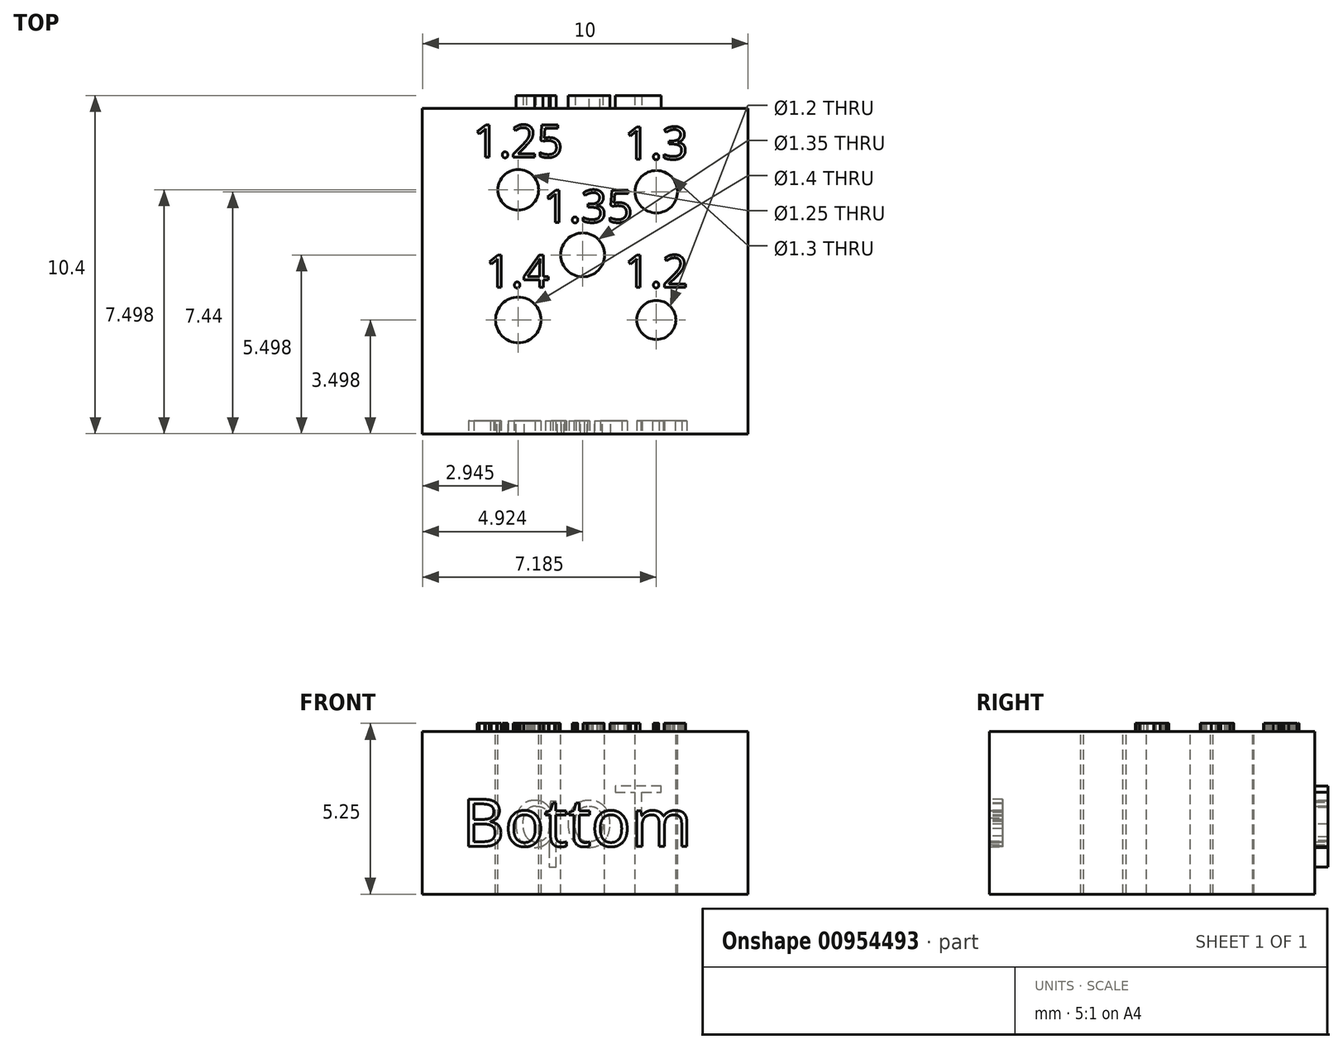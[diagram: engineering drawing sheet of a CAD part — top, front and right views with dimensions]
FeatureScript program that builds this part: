
annotation { "Feature Type Name" : "Feature", "Feature Type Description" : "" }
export const myFeature = defineFeature(function(context is Context, id is Id, definition is map)
    precondition{}
    {
        {
            var Q0;
            Q0=qCreatedBy(makeId("Top.planeOp"),FACE);
            var sketch = newSketch(context, id + "F0", { "sketchPlane" : qUnion([Q0])});
            skLineSegment(sketch, "E0.bottom", {"start": v(-5.65, 2.56) * mm, "end": v(4.35, 2.56) * mm});
            skLineSegment(sketch, "E0.top", {"start": v(-5.65, -7.44) * mm, "end": v(4.35, -7.44) * mm});
            skLineSegment(sketch, "E0.left", {"start": v(-5.65, 2.56) * mm, "end": v(-5.65, -7.44) * mm});
            skLineSegment(sketch, "E0.right", {"start": v(4.35, 2.56) * mm, "end": v(4.35, -7.44) * mm});
            skSolve(sketch);
        }
        {
            var Q0;
            Q0=makeQuery(id+"F0.imprint","IMPRINT",FACE,{"disambiguationData":[TD([[makeQuery(id+"F0.imprint","IMPRINT",EDGE,{"derivedFrom":sQuery(id+"F0.wireOp",EDGE,"E0.bottom")}),-1.0]])]});
            extrude(context, id + "F1", {"entities" : qUnion([Q0]), "depth" : 5 * mm, "offsetDistance" : 25 * mm});
        }
        {
            var Q0;
            Q0=makeQuery(id+"F1.opExtrude","CAP_FACE",FACE,{"disambiguationData":[OSD([sQuery(id+"F0.wireOp",EDGE,"E0.bottom"),sQuery(id+"F0.wireOp",EDGE,"E0.top"),sQuery(id+"F0.wireOp",EDGE,"E0.left"),sQuery(id+"F0.wireOp",EDGE,"E0.right")])],"isStart":false});
            var sketch = newSketch(context, id + "F2", { "sketchPlane" : qUnion([Q0])});
            skPoint(sketch, "E1", {"position": v(1.54, 0) * mm});
            skPoint(sketch, "E2", {"position": v(-2.7, -3.94) * mm});
            skPoint(sketch, "E3", {"position": v(1.54, -3.94) * mm});
            skPoint(sketch, "E4", {"position": v(-2.7, 0.06) * mm});
            skPoint(sketch, "E5", {"position": v(-0.73, -1.94) * mm});
            skCircle(sketch, "E6", {"center": v(-2.7, 0.06) * mm, "radius": 0.62 * mm});
            skCircle(sketch, "E7", {"center": v(1.54, 0) * mm, "radius": 0.65 * mm});
            skCircle(sketch, "E8", {"center": v(-0.73, -1.94) * mm, "radius": 0.68 * mm});
            skCircle(sketch, "E9", {"center": v(1.54, -3.94) * mm, "radius": 0.6 * mm});
            skCircle(sketch, "E10", {"center": v(-2.7, -3.94) * mm, "radius": 0.7 * mm});
            skText(sketch, "E11", { "text": "1.25\n", "fontName": "OpenSans-Regular.ttf"});
            skText(sketch, "E12", { "text": "1.3", "fontName": "OpenSans-Regular.ttf"});
            skText(sketch, "E13", { "text": "1.35", "fontName": "OpenSans-Regular.ttf"});
            skText(sketch, "E14", { "text": "1.4", "fontName": "OpenSans-Regular.ttf"});
            skText(sketch, "E15", { "text": "1.2", "fontName": "OpenSans-Regular.ttf"});
            const initialGuessF2  = {"E11": [-0.00409, 0.00106, 1, 0, 0.001], "E12": [0.00055, 0.001, 1, 0, 0.001], "E13": [-0.00194, -0.00094, 1, 0, 0.001], "E14": [-0.00372, -0.00294, 1, 0, 0.001], "E15": [0.00055, -0.00294, 1, 0, 0.001]};
            skSetInitialGuess(sketch, initialGuessF2);
            skSolve(sketch);
        }
        {
            var Q0;
            Q0=makeQuery(id+"F1.opExtrude","SWEPT_FACE",FACE,{"disambiguationData":[OSD([sQuery(id+"F0.wireOp",EDGE,"E0.bottom")])]});
            var sketch = newSketch(context, id + "F3", { "sketchPlane" : qUnion([Q0])});
            skText(sketch, "E16", { "text": "Top", "fontName": "OpenSans-Regular.ttf"});
            const initialGuessF3  = {"E16": [-0.0017, 0.00146, 1, 0, 0.00188]};
            skSetInitialGuess(sketch, initialGuessF3);
            skSolve(sketch);
        }
        {
            var Q0;
            Q0=makeQuery(id+"F1.opExtrude","SWEPT_FACE",FACE,{"disambiguationData":[OSD([sQuery(id+"F0.wireOp",EDGE,"E0.top")])]});
            var sketch = newSketch(context, id + "F4", { "sketchPlane" : qUnion([Q0])});
            skText(sketch, "E17", { "text": "Bottom\n", "fontName": "OpenSans-Regular.ttf"});
            const initialGuessF4  = {"E17": [-0.00444, 0.00147, 1, 0, 0.00146]};
            skSetInitialGuess(sketch, initialGuessF4);
            skSolve(sketch);
        }
        {
            var Q0;
            Q0=makeQuery(id+"F2.imprint","IMPRINT",FACE,{"disambiguationData":[TD([[makeQuery(id+"F2.imprint","IMPRINT",EDGE,{"derivedFrom":sQuery(id+"F2.wireOp",EDGE,"E9")}),1.0]])]});
            var Q1;
            Q1=makeQuery(id+"F2.imprint","IMPRINT",FACE,{"disambiguationData":[TD([[makeQuery(id+"F2.imprint","IMPRINT",EDGE,{"derivedFrom":sQuery(id+"F2.wireOp",EDGE,"E8")}),1.0]])]});
            var Q2;
            Q2=makeQuery(id+"F2.imprint","IMPRINT",FACE,{"disambiguationData":[TD([[makeQuery(id+"F2.imprint","IMPRINT",EDGE,{"derivedFrom":sQuery(id+"F2.wireOp",EDGE,"E10")}),1.0]])]});
            var Q3;
            Q3=makeQuery(id+"F2.imprint","IMPRINT",FACE,{"disambiguationData":[TD([[makeQuery(id+"F2.imprint","IMPRINT",EDGE,{"derivedFrom":sQuery(id+"F2.wireOp",EDGE,"E6")}),1.0]])]});
            var Q4;
            Q4=makeQuery(id+"F2.imprint","IMPRINT",FACE,{"disambiguationData":[TD([[makeQuery(id+"F2.imprint","IMPRINT",EDGE,{"derivedFrom":sQuery(id+"F2.wireOp",EDGE,"E7")}),1.0]])]});
            extrude(context, id + "F5", {"entities" : qUnion([Q0, Q1, Q2, Q3, Q4]), "operationType" : NewBodyOperationType.REMOVE, "oppositeDirection" : true, "depth" : 25 * mm, "offsetDistance" : 25 * mm});
        }
        {
            var Q0;
            Q0 = qSketchRegion(id + "F3", true);
            extrude(context, id + "F6", {"entities" : qUnion([Q0]), "operationType" : NewBodyOperationType.ADD, "depth" : .4 * mm, "offsetDistance" : 25 * mm});
        }
        {
            var Q0;
            Q0 = qSketchRegion(id + "F4", true);
            extrude(context, id + "F7", {"entities" : qUnion([Q0]), "operationType" : NewBodyOperationType.REMOVE, "oppositeDirection" : true, "depth" : .4 * mm, "offsetDistance" : 25 * mm});
        }
        {
            var Q0;
            Q0=makeQuery(id+"F2.imprint","IMPRINT",FACE,{"disambiguationData":[TD([[makeQuery(id+"F2.imprint","IMPRINT",EDGE,{"derivedFrom":sQuery(id+"F2.wireOp",EDGE,"E11.sketch_text.stroke-0")}),-1.0]])]});
            var Q1;
            Q1=makeQuery(id+"F2.imprint","IMPRINT",FACE,{"disambiguationData":[TD([[makeQuery(id+"F2.imprint","IMPRINT",EDGE,{"derivedFrom":sQuery(id+"F2.wireOp",EDGE,"E11.sketch_text.stroke-9")}),-1.0]])]});
            var Q2;
            Q2=makeQuery(id+"F2.imprint","IMPRINT",FACE,{"disambiguationData":[TD([[makeQuery(id+"F2.imprint","IMPRINT",EDGE,{"derivedFrom":sQuery(id+"F2.wireOp",EDGE,"E11.sketch_text.stroke-17")}),-1.0]])]});
            var Q3;
            Q3=makeQuery(id+"F2.imprint","IMPRINT",FACE,{"disambiguationData":[TD([[makeQuery(id+"F2.imprint","IMPRINT",EDGE,{"derivedFrom":sQuery(id+"F2.wireOp",EDGE,"E11.sketch_text.stroke-37")}),-1.0]])]});
            var Q4;
            Q4=makeQuery(id+"F2.imprint","IMPRINT",FACE,{"disambiguationData":[TD([[makeQuery(id+"F2.imprint","IMPRINT",EDGE,{"derivedFrom":sQuery(id+"F2.wireOp",EDGE,"E12.sketch_text.stroke-0")}),-1.0]])]});
            var Q5;
            Q5=makeQuery(id+"F2.imprint","IMPRINT",FACE,{"disambiguationData":[TD([[makeQuery(id+"F2.imprint","IMPRINT",EDGE,{"derivedFrom":sQuery(id+"F2.wireOp",EDGE,"E12.sketch_text.stroke-9")}),-1.0]])]});
            var Q6;
            Q6=makeQuery(id+"F2.imprint","IMPRINT",FACE,{"disambiguationData":[TD([[makeQuery(id+"F2.imprint","IMPRINT",EDGE,{"derivedFrom":sQuery(id+"F2.wireOp",EDGE,"E12.sketch_text.stroke-17")}),-1.0]])]});
            var Q7;
            Q7=makeQuery(id+"F2.imprint","IMPRINT",FACE,{"disambiguationData":[TD([[makeQuery(id+"F2.imprint","IMPRINT",EDGE,{"derivedFrom":sQuery(id+"F2.wireOp",EDGE,"E13.sketch_text.stroke-0")}),-1.0]])]});
            var Q8;
            Q8=makeQuery(id+"F2.imprint","IMPRINT",FACE,{"disambiguationData":[TD([[makeQuery(id+"F2.imprint","IMPRINT",EDGE,{"derivedFrom":sQuery(id+"F2.wireOp",EDGE,"E13.sketch_text.stroke-9")}),-1.0]])]});
            var Q9;
            Q9=makeQuery(id+"F2.imprint","IMPRINT",FACE,{"disambiguationData":[TD([[makeQuery(id+"F2.imprint","IMPRINT",EDGE,{"derivedFrom":sQuery(id+"F2.wireOp",EDGE,"E13.sketch_text.stroke-17")}),-1.0]])]});
            var Q10;
            Q10=makeQuery(id+"F2.imprint","IMPRINT",FACE,{"disambiguationData":[TD([[makeQuery(id+"F2.imprint","IMPRINT",EDGE,{"derivedFrom":sQuery(id+"F2.wireOp",EDGE,"E13.sketch_text.stroke-45")}),-1.0]])]});
            var Q11;
            Q11=makeQuery(id+"F2.imprint","IMPRINT",FACE,{"disambiguationData":[TD([[makeQuery(id+"F2.imprint","IMPRINT",EDGE,{"derivedFrom":sQuery(id+"F2.wireOp",EDGE,"E14.sketch_text.stroke-0")}),-1.0]])]});
            var Q12;
            Q12=makeQuery(id+"F2.imprint","IMPRINT",FACE,{"disambiguationData":[TD([[makeQuery(id+"F2.imprint","IMPRINT",EDGE,{"derivedFrom":sQuery(id+"F2.wireOp",EDGE,"E14.sketch_text.stroke-9")}),-1.0]])]});
            var Q13;
            Q13=makeQuery(id+"F2.imprint","IMPRINT",FACE,{"disambiguationData":[TD([[makeQuery(id+"F2.imprint","IMPRINT",EDGE,{"derivedFrom":sQuery(id+"F2.wireOp",EDGE,"E15.sketch_text.stroke-0")}),-1.0]])]});
            var Q14;
            Q14=makeQuery(id+"F2.imprint","IMPRINT",FACE,{"disambiguationData":[TD([[makeQuery(id+"F2.imprint","IMPRINT",EDGE,{"derivedFrom":sQuery(id+"F2.wireOp",EDGE,"E15.sketch_text.stroke-9")}),-1.0]])]});
            var Q15;
            Q15=makeQuery(id+"F2.imprint","IMPRINT",FACE,{"disambiguationData":[TD([[makeQuery(id+"F2.imprint","IMPRINT",EDGE,{"derivedFrom":sQuery(id+"F2.wireOp",EDGE,"E15.sketch_text.stroke-17")}),-1.0]])]});
            var Q16;
            Q16=makeQuery(id+"F2.imprint","IMPRINT",FACE,{"disambiguationData":[TD([[makeQuery(id+"F2.imprint","IMPRINT",EDGE,{"derivedFrom":sQuery(id+"F2.wireOp",EDGE,"E14.sketch_text.stroke-17")}),-1.0]])]});
            extrude(context, id + "F8", {"entities" : qUnion([Q0, Q1, Q2, Q3, Q4, Q5, Q6, Q7, Q8, Q9, Q10, Q11, Q12, Q13, Q14, Q15, Q16]), "operationType" : NewBodyOperationType.ADD, "depth" : 0.25 * mm, "offsetDistance" : 25 * mm});
        }
    });
